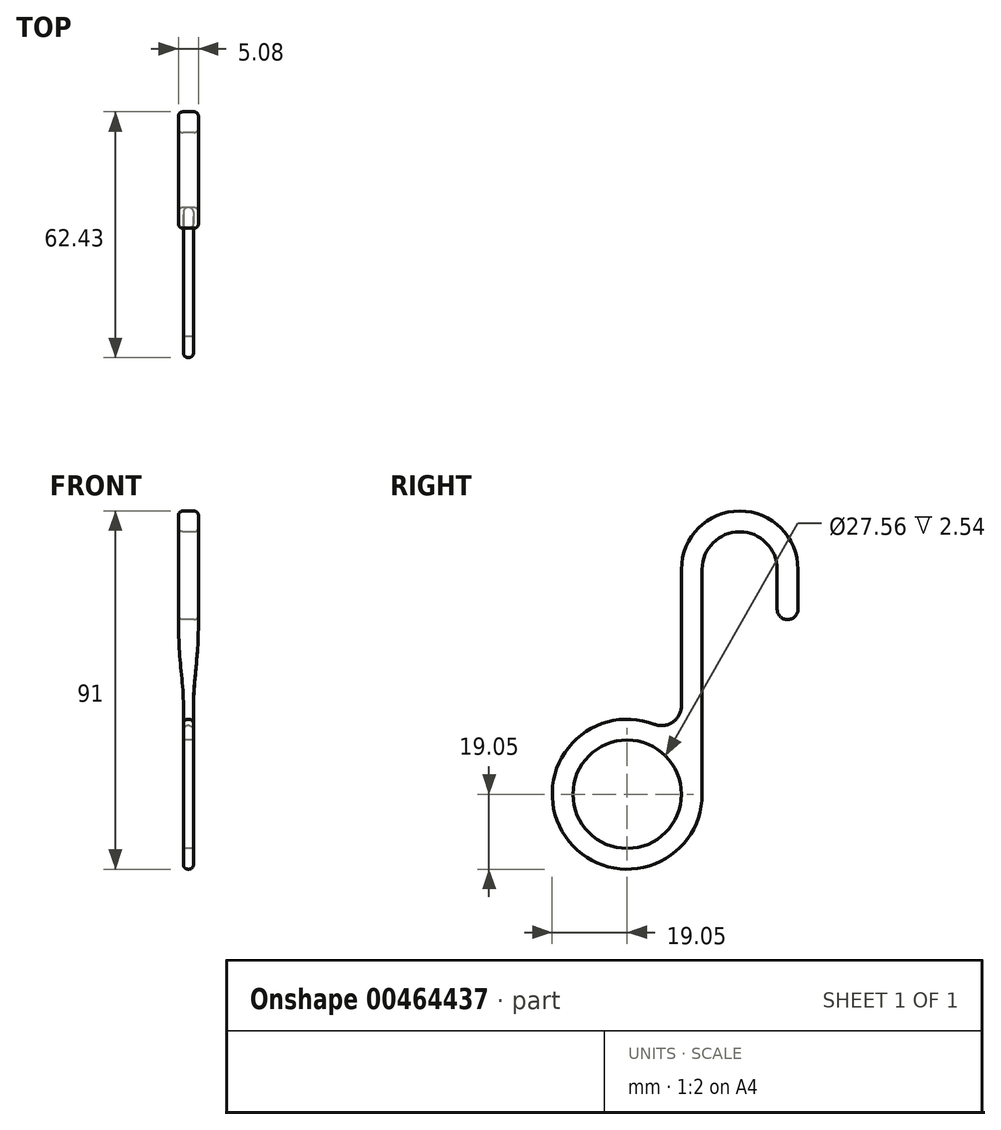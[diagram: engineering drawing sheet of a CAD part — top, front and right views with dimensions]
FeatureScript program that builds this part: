
annotation { "Feature Type Name" : "Feature", "Feature Type Description" : "" }
export const myFeature = defineFeature(function(context is Context, id is Id, definition is map)
    precondition{}
    {
        {
            var Q0;
            Q0=qCreatedBy(makeId("Right.planeOp"),FACE);
            var sketch = newSketch(context, id + "F0", { "sketchPlane" : qUnion([Q0])});
            skCircle(sketch, "E0", {"center": v(0, 0) * mm, "radius": 13.78 * mm});
            skCircle(sketch, "E1", {"center": v(0, 0) * mm, "radius": 19.05 * mm});
            skLineSegment(sketch, "E2", {"start": v(19.05, 0) * mm, "end": v(19.05, 57.15) * mm});
            skLineSegment(sketch, "E3", {"start": v(13.78, 0) * mm, "end": v(13.78, 57.15) * mm});
            skPoint(sketch, "E4", {"position": v(0, 19.05) * mm});
            skArc(sketch, "E5", {"start": v(43.38, 57.15) * mm, "mid": v(28.58, 71.95) * mm, "end": v(13.78, 57.15) * mm});
            skArc(sketch, "E6", {"start": v(38.1, 57.15) * mm, "mid": v(28.57, 66.68) * mm, "end": v(19.05, 57.15) * mm});
            skLineSegment(sketch, "E7", {"start": v(38.1, 57.15) * mm, "end": v(38.1, 47) * mm});
            skLineSegment(sketch, "E8", {"start": v(43.38, 57.15) * mm, "end": v(43.38, 47) * mm});
            skArc(sketch, "E9", {"start": v(38.1, 47) * mm, "mid": v(40.74, 44.35) * mm, "end": v(43.38, 47) * mm});
            skSolve(sketch);
        }
        {
            var Q0;
            Q0=makeQuery(id+"F0.imprint","IMPRINT",FACE,{"disambiguationData":[TD([[makeQuery(id+"F0.imprint","IMPRINT",EDGE,{"derivedFrom":sQuery(id+"F0.wireOp",EDGE,"E0")}),-1.0]])]});
            var Q1;
            {var subQ4=sQuery(id+"F0.wireOp",EDGE,"E2");Q1=makeQuery(id+"F0.imprint","IMPRINT",FACE,{"disambiguationData":[TD([[makeQuery(id+"F0.imprint","IMPRINT",EDGE,{"derivedFrom":subQ4}),1.0]])]});}
            extrude(context, id + "F1", {"entities" : qUnion([Q0, Q1]), "depth" : 2.54 * mm});
        }
        {
            var Q0;
            Q0=makeQuery(id+"F1.opExtrude","SWEPT_EDGE",EDGE,{"disambiguationData":[OSD([sQuery(id+"F0.wireOp",EDGE,"E1"),sQuery(id+"F0.wireOp",EDGE,"E3")])]});
            fillet(context, id + "F2", {"entities" : qUnion([Q0]), "radius" : 5.08 * mm, "tangentPropagation" : true, "allowEdgeOverflow" : false});
        }
        {
            var Q0;
            Q0=makeQuery(id+"F1.opExtrude","CAP_FACE",FACE,{"disambiguationData":[OSD([sQuery(id+"F0.wireOp",EDGE,"E0"),sQuery(id+"F0.wireOp",EDGE,"E1"),sQuery(id+"F0.wireOp",EDGE,"E2"),sQuery(id+"F0.wireOp",EDGE,"E3"),sQuery(id+"F0.wireOp",EDGE,"E5"),sQuery(id+"F0.wireOp",EDGE,"E6"),sQuery(id+"F0.wireOp",EDGE,"E7"),sQuery(id+"F0.wireOp",EDGE,"E8"),sQuery(id+"F0.wireOp",EDGE,"E9")])],"isStart":false});
            var sketch = newSketch(context, id + "F3", { "sketchPlane" : qUnion([Q0])});
            skLineSegment(sketch, "E10", {"start": v(19.05, 44.88) * mm, "end": v(13.78, 44.88) * mm});
            skSolve(sketch);
        }
        {
            var Q0;
            {var subQ2=sQuery(id+"F3.wireOp",EDGE,"E10");Q0=makeQuery(id+"F3.imprint","IMPRINT",FACE,{"disambiguationData":[TD([[makeQuery(id+"F3.imprint","IMPRINT",EDGE,{"derivedFrom":subQ2}),-1.0]])]});}
            extrude(context, id + "F4", {"entities" : qUnion([Q0]), "operationType" : NewBodyOperationType.ADD, "depth" : 1.27 * mm});
        }
        {
            var Q0;
            Q0=makeQuery(id+"F1.opExtrude","CAP_FACE",FACE,{"disambiguationData":[OSD([sQuery(id+"F0.wireOp",EDGE,"E0"),sQuery(id+"F0.wireOp",EDGE,"E1"),sQuery(id+"F0.wireOp",EDGE,"E2"),sQuery(id+"F0.wireOp",EDGE,"E3"),sQuery(id+"F0.wireOp",EDGE,"E5"),sQuery(id+"F0.wireOp",EDGE,"E6"),sQuery(id+"F0.wireOp",EDGE,"E7"),sQuery(id+"F0.wireOp",EDGE,"E8"),sQuery(id+"F0.wireOp",EDGE,"E9")])],"isStart":true});
            var sketch = newSketch(context, id + "F5", { "sketchPlane" : qUnion([Q0])});
            skLineSegment(sketch, "E11.0", {"start": v(-19.05, 44.88) * mm, "end": v(-13.78, 44.88) * mm});
            skSolve(sketch);
        }
        {
            var Q0;
            {var subQ2=sQuery(id+"F5.wireOp",EDGE,"E11.0");Q0=makeQuery(id+"F5.imprint","IMPRINT",FACE,{"disambiguationData":[TD([[makeQuery(id+"F5.imprint","IMPRINT",EDGE,{"derivedFrom":subQ2}),1.0]])]});}
            extrude(context, id + "F6", {"entities" : qUnion([Q0]), "operationType" : NewBodyOperationType.ADD, "depth" : 1.27 * mm});
        }
        {
            var Q0;
            {var subQ0=sQuery(id+"F0.wireOp",EDGE,"E3");Q0=makeQuery(id+"F6.boolean.opBoolean","MERGE",FACE,{"derivedFrom":[makeQuery(id+"F4.boolean.opBoolean","MERGE",FACE,{"derivedFrom":[makeQuery(id+"F1.opExtrude","SWEPT_FACE",FACE,{"disambiguationData":[OSD([subQ0])]}),makeQuery(id+"F4.opExtrude","SWEPT_FACE",FACE,{"disambiguationData":[OSD([subQ0])]})]}),makeQuery(id+"F6.opExtrude","SWEPT_FACE",FACE,{"disambiguationData":[OSD([subQ0])]})]});}
            var sketch = newSketch(context, id + "F7", { "sketchPlane" : qUnion([Q0])});
            skLineSegment(sketch, "E12", {"start": v(1.27, 46.07) * mm, "end": v(1.27, 22.5) * mm, "construction": true});
            skFitSpline(sketch, "E13", {"points": [v(-1.27, 44.88) * mm, v(-1.05, 36.8) * mm, v(-0.66, 32.17) * mm, v(0, 22.5) * mm], "startDerivative": vector(0, -25.12) * mm, "endDerivative": vector(0, -23.7) * mm});
            skFitSpline(sketch, "E14.MirrorCS", {"points": [v(3.8, 44.88) * mm, v(3.59, 36.8) * mm, v(3.2, 32.17) * mm, v(2.54, 22.5) * mm], "startDerivative": vector(0, -25.12) * mm, "endDerivative": vector(0, -23.7) * mm});
            skSolve(sketch);
        }
        {
            var Q0;
            Q0=makeQuery(id+"F7.imprint","IMPRINT",FACE,{"disambiguationData":[TD([[makeQuery(id+"F7.imprint","IMPRINT",EDGE,{"derivedFrom":sQuery(id+"F7.wireOp",EDGE,"E13")}),1.0]])]});
            var Q1;
            Q1=makeQuery(id+"F7.imprint","IMPRINT",FACE,{"disambiguationData":[TD([[makeQuery(id+"F7.imprint","IMPRINT",EDGE,{"derivedFrom":sQuery(id+"F7.wireOp",EDGE,"E14.MirrorCS")}),-1.0]])]});
            var Q2;
            {var subQ0=sQuery(id+"F0.wireOp",EDGE,"E2");Q2=makeQuery(id+"F6.boolean.opBoolean","MERGE",FACE,{"derivedFrom":[makeQuery(id+"F4.boolean.opBoolean","MERGE",FACE,{"derivedFrom":[makeQuery(id+"F1.opExtrude","SWEPT_FACE",FACE,{"disambiguationData":[OSD([subQ0])]}),makeQuery(id+"F4.opExtrude","SWEPT_FACE",FACE,{"disambiguationData":[OSD([subQ0])]})]}),makeQuery(id+"F6.opExtrude","SWEPT_FACE",FACE,{"disambiguationData":[OSD([subQ0])]})]});}
            extrude(context, id + "F8", {"entities" : qUnion([Q0, Q1]), "operationType" : NewBodyOperationType.ADD, "endBound" : BoundingType.UP_TO_SURFACE, "oppositeDirection" : true, "endBoundEntityFace" : qUnion([Q2]), "depth" : 25.4 * mm});
        }
        {
            var Q0;
            Q0=makeQuery(id+"F6.opExtrude","CAP_EDGE",EDGE,{"disambiguationData":[OSD([sQuery(id+"F0.wireOp",EDGE,"E6")])],"isStart":false});
            var Q1;
            Q1=makeQuery(id+"F4.opExtrude","CAP_EDGE",EDGE,{"disambiguationData":[OSD([sQuery(id+"F0.wireOp",EDGE,"E5")])],"isStart":false});
            fillet(context, id + "F9", {"entities" : qUnion([Q0, Q1]), "radius" : 1.14 * mm, "tangentPropagation" : true, "allowEdgeOverflow" : false});
        }
    });
